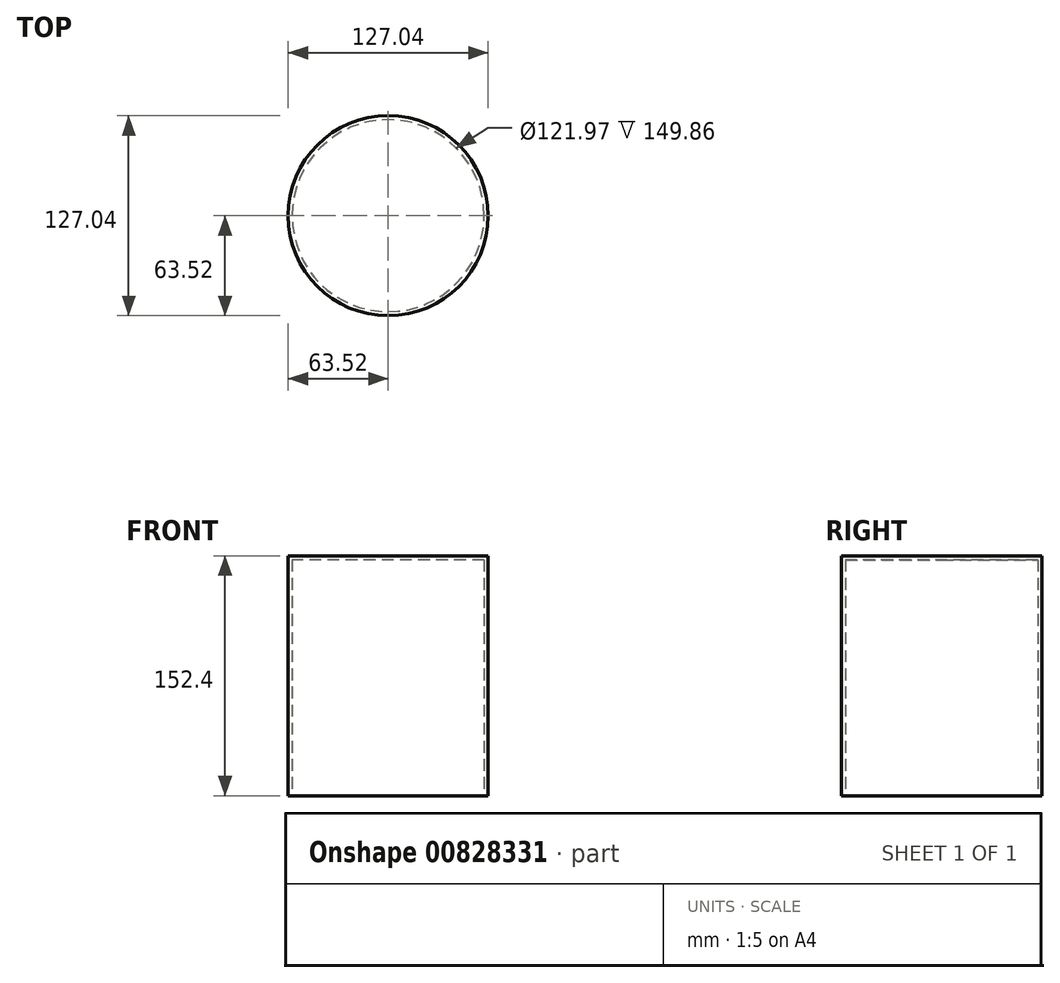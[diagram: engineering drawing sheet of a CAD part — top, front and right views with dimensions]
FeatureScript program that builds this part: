
annotation { "Feature Type Name" : "Feature", "Feature Type Description" : "" }
export const myFeature = defineFeature(function(context is Context, id is Id, definition is map)
    precondition{}
    {
        {
            var Q0;
            Q0=qCreatedBy(makeId("Top.planeOp"),FACE);
            var sketch = newSketch(context, id + "F0", { "sketchPlane" : qUnion([Q0])});
            skCircle(sketch, "E0", {"center": v(0, 0) * mm, "radius": 63.52 * mm});
            skSolve(sketch);
        }
        {
            var Q0;
            Q0=makeQuery(id+"F0.imprint","IMPRINT",FACE,{"disambiguationData":[TD([[makeQuery(id+"F0.imprint","IMPRINT",EDGE,{"derivedFrom":sQuery(id+"F0.wireOp",EDGE,"E0")}),1.0]])]});
            extrude(context, id + "F1", {"entities" : qUnion([Q0]), "depth" : 152.4 * mm, "offsetDistance" : 25.4 * mm});
        }
        {
            var Q0;
            Q0=makeQuery(id+"F1.opExtrude","CAP_FACE",FACE,{"disambiguationData":[OSD([sQuery(id+"F0.wireOp",EDGE,"E0")])],"isStart":true});
            shell(context, id + "F2", {"entities" : qUnion([Q0]), "thickness" : 2.54 * mm});
        }
    });
